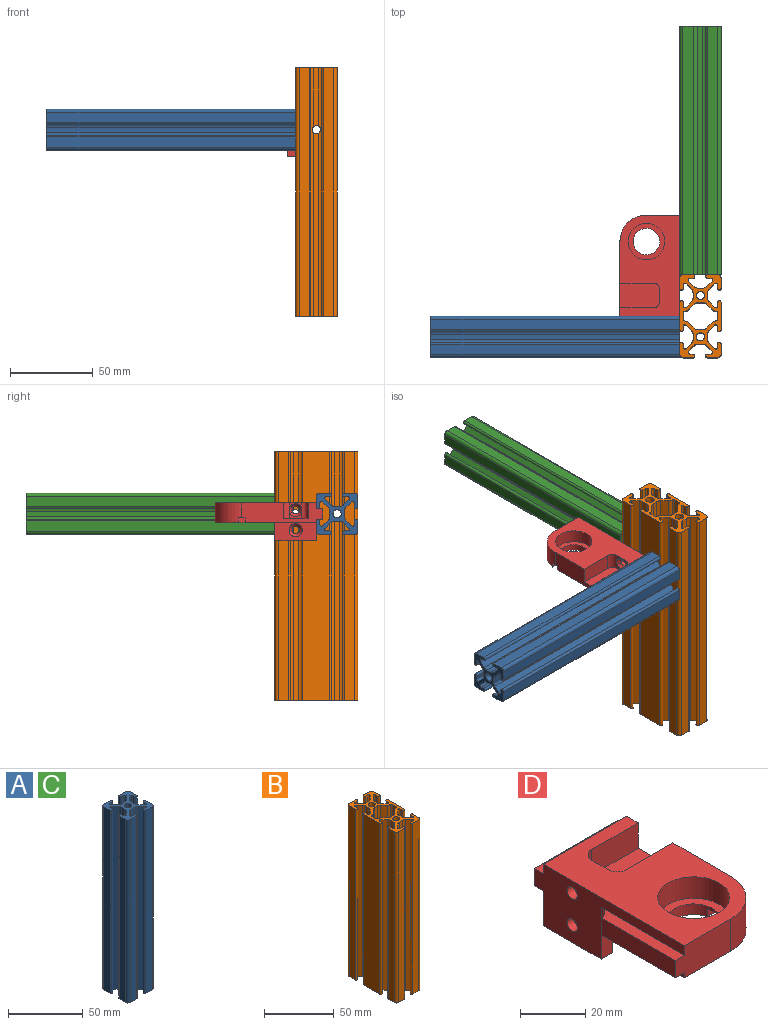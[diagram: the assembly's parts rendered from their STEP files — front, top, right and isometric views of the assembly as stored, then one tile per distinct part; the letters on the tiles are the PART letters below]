
ASSEMBLY  parts=4 mates=3
PART A: 59 faces, bbox 25x25x150 mm
  f0: plane 150x3.2mm, normal (-0.71,-0.71,0), area 679.2mm2, adj f28,f30,f57,f58
  f1: plane 150x2.08mm, normal (1,0,0), area 311.5mm2, adj f28,f29,f57,f58
  f2: plane 150x6.22mm, normal (-1,0,0), area 932.6mm2, adj f29,f55,f57,f58
  f3: plane 150x3.11mm, normal (-1,0,0), area 466.6mm2, adj f30,f31,f57,f58
  f4: plane 150x3.2mm, normal (-0.71,0.71,0), area 679.2mm2, adj f31,f32,f57,f58
  f5: plane 150x2.08mm, normal (1,0,0), area 311.5mm2, adj f32,f33,f57,f58
  f6: plane 150x6.22mm, normal (-1,0,0), area 932.6mm2, adj f33,f34,f57,f58
  f7: plane 150x6.15mm, normal (0,-1,0), area 922.4mm2, adj f34,f35,f57,f58
  f8: plane 150x2.03mm, normal (0,1,0), area 304.8mm2, adj f35,f36,f57,f58
  f9: plane 150x3.34mm, normal (0.71,-0.71,0), area 707.7mm2, adj f36,f37,f57,f58
  f10: plane 150x3.11mm, normal (0,-1,0), area 466.6mm2, adj f37,f38,f57,f58
  f11: plane 150x3.34mm, normal (-0.71,-0.71,0), area 707.7mm2, adj f38,f39,f57,f58
  f12: plane 150x2.03mm, normal (0,1,0), area 304.8mm2, adj f39,f40,f57,f58
  f13: plane 150x6.15mm, normal (0,-1,0), area 922.4mm2, adj f40,f41,f57,f58
  f14: plane 150x6.22mm, normal (1,0,0), area 932.6mm2, adj f41,f42,f57,f58
  f15: plane 150x2.08mm, normal (-1,0,0), area 311.5mm2, adj f42,f43,f57,f58
  f16: plane 150x3.2mm, normal (0.71,0.71,0), area 679.2mm2, adj f43,f44,f57,f58
  f17: plane 150x3.11mm, normal (1,0,0), area 466.6mm2, adj f44,f45,f57,f58
  f18: plane 150x3.2mm, normal (0.71,-0.71,0), area 679.2mm2, adj f45,f46,f57,f58
  f19: plane 150x2.08mm, normal (-1,0,0), area 311.5mm2, adj f46,f47,f57,f58
  f20: plane 150x6.22mm, normal (1,0,0), area 932.6mm2, adj f47,f48,f57,f58
  f21: plane 150x6.22mm, normal (0,1,0), area 932.6mm2, adj f48,f49,f57,f58
  f22: plane 150x2.1mm, normal (0,-1,0), area 315mm2, adj f49,f50,f57,f58
  f23: plane 150x3.34mm, normal (-0.71,0.71,0), area 707.7mm2, adj f50,f51,f57,f58
  f24: plane 150x3.11mm, normal (0,1,0), area 466.6mm2, adj f51,f52,f57,f58
  f25: plane 150x3.34mm, normal (0.71,0.71,0), area 707.7mm2, adj f52,f53,f57,f58
  f26: plane 150x2.1mm, normal (0,-1,0), area 315mm2, adj f53,f54,f57,f58
  f27: plane 150x6.22mm, normal (0,1,0), area 932.6mm2, adj f54,f55,f57,f58
  f28: cylinder r=1.01mm len=150mm, axis (0,0,-1), area 356.9mm2, adj f0,f1,f57,f58
  f29: cylinder r=1.07mm len=150mm, axis (0,0,-1), area 504.2mm2, adj f1,f2,f57,f58
  f30: cylinder r=3.33mm len=150mm, axis (0,0,-1), area 392.7mm2, adj f0,f3,f57,f58
  f31: cylinder r=3.33mm len=150mm, axis (0,0,-1), area 392.7mm2, adj f3,f4,f57,f58
  f32: cylinder r=1.01mm len=150mm, axis (0,0,-1), area 356.9mm2, adj f4,f5,f57,f58
  f33: cylinder r=1.07mm len=150mm, axis (0,0,-1), area 504.2mm2, adj f5,f6,f57,f58
  f34: cylinder r=1.96mm len=150mm, axis (0,0,-1), area 462.5mm2, adj f6,f7,f57,f58
  f35: cylinder r=1.07mm len=150mm, axis (0,0,-1), area 504.2mm2, adj f7,f8,f57,f58
  f36: cylinder r=1.01mm len=150mm, axis (0,0,-1), area 357.1mm2, adj f8,f9,f57,f58
  f37: cylinder r=3.17mm len=150mm, axis (0,0,-1), area 373.1mm2, adj f9,f10,f57,f58
  f38: cylinder r=3.17mm len=150mm, axis (0,0,-1), area 373.1mm2, adj f10,f11,f57,f58
  f39: cylinder r=1.01mm len=150mm, axis (0,0,-1), area 357.1mm2, adj f11,f12,f57,f58
  f40: cylinder r=1.07mm len=150mm, axis (0,0,-1), area 504.2mm2, adj f12,f13,f57,f58
  f41: cylinder r=1.96mm len=150mm, axis (0,0,-1), area 462.5mm2, adj f13,f14,f57,f58
  f42: cylinder r=1.07mm len=150mm, axis (0,0,-1), area 504.2mm2, adj f14,f15,f57,f58
  f43: cylinder r=1.01mm len=150mm, axis (0,0,-1), area 356.9mm2, adj f15,f16,f57,f58
  f44: cylinder r=3.33mm len=150mm, axis (0,0,-1), area 392.7mm2, adj f16,f17,f57,f58
  f45: cylinder r=3.33mm len=150mm, axis (0,0,-1), area 392.7mm2, adj f17,f18,f57,f58
  f46: cylinder r=1.01mm len=150mm, axis (0,0,-1), area 356.9mm2, adj f18,f19,f57,f58
  f47: cylinder r=1.07mm len=150mm, axis (0,0,-1), area 504.2mm2, adj f19,f20,f57,f58
  f48: cylinder r=1.96mm len=150mm, axis (0,0,-1), area 462.5mm2, adj f20,f21,f57,f58
  f49: cylinder r=1.07mm len=150mm, axis (0,0,-1), area 504.2mm2, adj f21,f22,f57,f58
  f50: cylinder r=1.01mm len=150mm, axis (0,0,-1), area 357.1mm2, adj f22,f23,f57,f58
  f51: cylinder r=3.17mm len=150mm, axis (0,0,-1), area 373.1mm2, adj f23,f24,f57,f58
  f52: cylinder r=3.17mm len=150mm, axis (0,0,-1), area 373.1mm2, adj f24,f25,f57,f58
  f53: cylinder r=1.01mm len=150mm, axis (0,0,-1), area 357.1mm2, adj f25,f26,f57,f58
  f54: cylinder r=1.07mm len=150mm, axis (0,0,-1), area 504.2mm2, adj f26,f27,f57,f58
  f55: cylinder r=1.96mm len=150mm, axis (0,0,-1), area 462.5mm2, adj f2,f27,f57,f58
  f56: cylinder r=2.5mm len=150mm, axis (0,0,-1), area 2356.2mm2, adj f57,f58
  f57: plane 25x25mm, normal (0,0,1), area 274.7mm2, adj f0,f1,f2,f3,f4,f5,f6,f7
  f58: plane 25x25mm, normal (0,0,-1), area 274.7mm2, adj f0,f1,f2,f3,f4,f5,f6,f7
PART B: 126 faces, bbox 25x50x150 mm
  f0: plane 110.56x3.15mm, normal (0,1,0), area 346.8mm2, adj f90,f91,f123,f124
  f1: plane 110.56x3.15mm, normal (0,-1,0), area 346.8mm2, adj f103,f104,f122,f124
  f2: plane 110.56x3.15mm, normal (-1,0,0), area 346.8mm2, adj f57,f58,f117,f124
  f3: plane 110.56x3.15mm, normal (-1,0,0), area 346.8mm2, adj f63,f64,f119,f124
  f4: plane 150x0.24mm, normal (0,-1,0), area 36.3mm2, adj f54,f105,f124,f125
  f5: plane 150x4.34mm, normal (1,0,0), area 651mm2, adj f54,f95,f124,f125
  f6: plane 150x6.15mm, normal (-1,0,0), area 922.3mm2, adj f55,f94,f124,f125
  f7: plane 150x2.11mm, normal (1,0,0), area 316.2mm2, adj f55,f56,f124,f125
  f8: plane 150x3.32mm, normal (-0.71,-0.71,0), area 704.6mm2, adj f56,f57,f124,f125
  f9: plane 150x3.32mm, normal (-0.71,0.71,0), area 704.6mm2, adj f58,f59,f124,f125
  f10: plane 150x2.11mm, normal (1,0,0), area 316.2mm2, adj f59,f60,f124,f125
  f11: plane 150x16.36mm, normal (-1,0,0), area 2454mm2, adj f60,f61,f124,f125
  f12: plane 150x2.11mm, normal (1,0,0), area 316.2mm2, adj f61,f62,f124,f125
  f13: plane 150x3.32mm, normal (-0.71,-0.71,0), area 704.6mm2, adj f62,f63,f124,f125
  f14: plane 150x3.32mm, normal (-0.71,0.71,0), area 704.6mm2, adj f64,f65,f124,f125
  f15: plane 150x2.11mm, normal (1,0,0), area 316.2mm2, adj f65,f66,f124,f125
  f16: plane 150x6.15mm, normal (-1,0,0), area 922.3mm2, adj f66,f67,f124,f125
  f17: plane 150x6.15mm, normal (0,-1,0), area 922.3mm2, adj f67,f68,f124,f125
  f18: plane 150x2.11mm, normal (0,1,0), area 316.2mm2, adj f68,f69,f124,f125
  f19: plane 150x3.32mm, normal (0.71,-0.71,0), area 704.6mm2, adj f69,f70,f124,f125
  f20: plane 110.56x3.15mm, normal (0,-1,0), area 346.8mm2, adj f70,f71,f120,f124
  f21: plane 150x3.32mm, normal (-0.71,-0.71,0), area 704.6mm2, adj f71,f72,f124,f125
  f22: plane 150x2.11mm, normal (0,1,0), area 316.2mm2, adj f72,f73,f124,f125
  f23: plane 150x6.15mm, normal (0,-1,0), area 922.3mm2, adj f73,f74,f124,f125
  f24: plane 150x6.15mm, normal (1,0,0), area 922.3mm2, adj f74,f75,f124,f125
  f25: plane 150x2.11mm, normal (-1,0,0), area 316.2mm2, adj f75,f76,f124,f125
  f26: plane 150x3.32mm, normal (0.71,0.71,0), area 704.6mm2, adj f76,f77,f124,f125
  f27: plane 110.56x3.15mm, normal (1,0,0), area 346.8mm2, adj f77,f78,f118,f124
  f28: plane 150x3.32mm, normal (0.71,-0.71,0), area 704.6mm2, adj f78,f79,f124,f125
  f29: plane 150x2.11mm, normal (-1,0,0), area 316.2mm2, adj f79,f80,f124,f125
  f30: plane 150x16.36mm, normal (1,0,0), area 2454mm2, adj f80,f81,f124,f125
  f31: plane 150x2.11mm, normal (-1,0,0), area 316.2mm2, adj f81,f82,f124,f125
  f32: plane 150x3.32mm, normal (0.71,0.71,0), area 704.6mm2, adj f82,f83,f124,f125
  f33: plane 110.56x3.15mm, normal (1,0,0), area 346.8mm2, adj f83,f84,f116,f124
  f34: plane 150x3.32mm, normal (0.71,-0.71,0), area 704.6mm2, adj f84,f85,f124,f125
  f35: plane 150x2.11mm, normal (-1,0,0), area 316.2mm2, adj f85,f86,f124,f125
  f36: plane 150x6.15mm, normal (1,0,0), area 922.3mm2, adj f86,f87,f124,f125
  f37: plane 150x6.15mm, normal (0,1,0), area 922.3mm2, adj f87,f88,f124,f125
  f38: plane 150x2.11mm, normal (0,-1,0), area 316.2mm2, adj f88,f89,f124,f125
  f39: plane 150x3.32mm, normal (-0.71,0.71,0), area 704.6mm2, adj f89,f90,f124,f125
  f40: plane 150x3.32mm, normal (0.71,0.71,0), area 704.6mm2, adj f91,f92,f124,f125
  f41: plane 150x2.11mm, normal (0,-1,0), area 316.2mm2, adj f92,f93,f124,f125
  f42: plane 150x6.15mm, normal (0,1,0), area 922.3mm2, adj f93,f94,f124,f125
  f43: plane 150x0.24mm, normal (0,1,0), area 36.3mm2, adj f95,f96,f124,f125
  f44: plane 150x3.32mm, normal (0.71,0.71,0), area 704.6mm2, adj f96,f97,f124,f125
  f45: plane 110.56x3.15mm, normal (0,1,0), area 346.8mm2, adj f97,f98,f121,f124
  f46: plane 150x3.32mm, normal (-0.71,0.71,0), area 704.6mm2, adj f98,f99,f124,f125
  f47: plane 150x0.24mm, normal (0,1,0), area 36.3mm2, adj f99,f100,f124,f125
  f48: plane 150x4.34mm, normal (-1,0,0), area 651mm2, adj f100,f101,f124,f125
  f49: plane 150x0.24mm, normal (0,-1,0), area 36.3mm2, adj f101,f102,f124,f125
  f50: plane 150x3.32mm, normal (-0.71,-0.71,0), area 704.6mm2, adj f102,f103,f124,f125
  f51: plane 150x3.32mm, normal (0.71,-0.71,0), area 704.6mm2, adj f104,f105,f124,f125
  f52: cylinder r=2.5mm len=110.73mm, axis (0,0,-1), area 1731.8mm2, adj f118,f119,f120,f121,f124
  f53: cylinder r=2.5mm len=110.73mm, axis (0,0,-1), area 1731.8mm2, adj f116,f117,f122,f123,f124
  f54: cylinder r=0.76mm len=150mm, axis (0,0,-1), area 179.1mm2, adj f4,f5,f124,f125
  f55: cylinder r=1.07mm len=150mm, axis (0,0,-1), area 504.2mm2, adj f6,f7,f124,f125
  f56: cylinder r=1mm len=150mm, axis (0,0,-1), area 354.1mm2, adj f7,f8,f124,f125
  f57: cylinder r=3.17mm len=150mm, axis (0,0,-1), area 370.9mm2, adj f2,f8,f110,f117,f124,f125
  f58: cylinder r=3.17mm len=150mm, axis (0,0,-1), area 370.9mm2, adj f2,f9,f110,f117,f124,f125
  f59: cylinder r=1mm len=150mm, axis (0,0,-1), area 354.1mm2, adj f9,f10,f124,f125
  f60: cylinder r=1.07mm len=150mm, axis (0,0,-1), area 504.2mm2, adj f10,f11,f124,f125
  f61: cylinder r=1.07mm len=150mm, axis (0,0,-1), area 504.2mm2, adj f11,f12,f124,f125
  f62: cylinder r=1mm len=150mm, axis (0,0,-1), area 354.1mm2, adj f12,f13,f124,f125
  f63: cylinder r=3.17mm len=150mm, axis (0,0,-1), area 370.9mm2, adj f3,f13,f111,f119,f124,f125
  f64: cylinder r=3.17mm len=150mm, axis (0,0,-1), area 370.9mm2, adj f3,f14,f111,f119,f124,f125
  f65: cylinder r=1mm len=150mm, axis (0,0,-1), area 354.1mm2, adj f14,f15,f124,f125
  f66: cylinder r=1.07mm len=150mm, axis (0,0,-1), area 504.2mm2, adj f15,f16,f124,f125
  f67: cylinder r=2.03mm len=150mm, axis (0,0,-1), area 478.6mm2, adj f16,f17,f124,f125
  f68: cylinder r=1.07mm len=150mm, axis (0,0,-1), area 504.2mm2, adj f17,f18,f124,f125
  f69: cylinder r=1mm len=150mm, axis (0,0,-1), area 354.1mm2, adj f18,f19,f124,f125
  f70: cylinder r=3.17mm len=150mm, axis (0,0,-1), area 370.9mm2, adj f19,f20,f106,f120,f124,f125
  f71: cylinder r=3.17mm len=150mm, axis (0,0,-1), area 370.9mm2, adj f20,f21,f106,f120,f124,f125
  f72: cylinder r=1mm len=150mm, axis (0,0,-1), area 354.1mm2, adj f21,f22,f124,f125
  f73: cylinder r=1.07mm len=150mm, axis (0,0,-1), area 504.2mm2, adj f22,f23,f124,f125
  f74: cylinder r=2.03mm len=150mm, axis (0,0,-1), area 478.6mm2, adj f23,f24,f124,f125
  f75: cylinder r=1.07mm len=150mm, axis (0,0,-1), area 504.2mm2, adj f24,f25,f124,f125
  f76: cylinder r=1mm len=150mm, axis (0,0,-1), area 354.1mm2, adj f25,f26,f124,f125
  f77: cylinder r=3.17mm len=150mm, axis (0,0,-1), area 370.9mm2, adj f26,f27,f108,f118,f124,f125
  f78: cylinder r=3.17mm len=150mm, axis (0,0,-1), area 370.9mm2, adj f27,f28,f108,f118,f124,f125
  f79: cylinder r=1mm len=150mm, axis (0,0,-1), area 354.1mm2, adj f28,f29,f124,f125
  f80: cylinder r=1.07mm len=150mm, axis (0,0,-1), area 504.2mm2, adj f29,f30,f124,f125
  f81: cylinder r=1.07mm len=150mm, axis (0,0,-1), area 504.2mm2, adj f30,f31,f124,f125
  f82: cylinder r=1mm len=150mm, axis (0,0,-1), area 354.1mm2, adj f31,f32,f124,f125
  f83: cylinder r=3.17mm len=150mm, axis (0,0,-1), area 370.9mm2, adj f32,f33,f109,f116,f124,f125
  f84: cylinder r=3.17mm len=150mm, axis (0,0,-1), area 370.9mm2, adj f33,f34,f109,f116,f124,f125
  f85: cylinder r=1mm len=150mm, axis (0,0,-1), area 354.1mm2, adj f34,f35,f124,f125
  f86: cylinder r=1.07mm len=150mm, axis (0,0,-1), area 504.2mm2, adj f35,f36,f124,f125
  f87: cylinder r=2.03mm len=150mm, axis (0,0,-1), area 478.6mm2, adj f36,f37,f124,f125
  f88: cylinder r=1.07mm len=150mm, axis (0,0,-1), area 504.2mm2, adj f37,f38,f124,f125
  f89: cylinder r=1mm len=150mm, axis (0,0,-1), area 354.1mm2, adj f38,f39,f124,f125
  f90: cylinder r=3.17mm len=150mm, axis (0,0,-1), area 370.9mm2, adj f0,f39,f112,f123,f124,f125
  f91: cylinder r=3.17mm len=150mm, axis (0,0,-1), area 370.9mm2, adj f0,f40,f112,f123,f124,f125
  f92: cylinder r=1mm len=150mm, axis (0,0,-1), area 354.1mm2, adj f40,f41,f124,f125
  f93: cylinder r=1.07mm len=150mm, axis (0,0,-1), area 504.2mm2, adj f41,f42,f124,f125
  f94: cylinder r=2.03mm len=150mm, axis (0,0,-1), area 478.6mm2, adj f6,f42,f124,f125
  f95: cylinder r=0.76mm len=150mm, axis (0,0,-1), area 179.1mm2, adj f5,f43,f124,f125
  f96: cylinder r=3.14mm len=150mm, axis (0,0,-1), area 370.1mm2, adj f43,f44,f124,f125
  f97: cylinder r=3.17mm len=150mm, axis (0,0,-1), area 370.9mm2, adj f44,f45,f107,f121,f124,f125
  f98: cylinder r=3.17mm len=150mm, axis (0,0,-1), area 370.9mm2, adj f45,f46,f107,f121,f124,f125
  f99: cylinder r=3.14mm len=150mm, axis (0,0,-1), area 370.1mm2, adj f46,f47,f124,f125
  f100: cylinder r=0.76mm len=150mm, axis (0,0,-1), area 179.1mm2, adj f47,f48,f124,f125
  f101: cylinder r=0.76mm len=150mm, axis (0,0,-1), area 179.1mm2, adj f48,f49,f124,f125
  f102: cylinder r=3.14mm len=150mm, axis (0,0,-1), area 370.1mm2, adj f49,f50,f124,f125
  f103: cylinder r=3.17mm len=150mm, axis (0,0,-1), area 370.9mm2, adj f1,f50,f115,f122,f124,f125
  f104: cylinder r=3.17mm len=150mm, axis (0,0,-1), area 370.9mm2, adj f1,f51,f115,f122,f124,f125
  f105: cylinder r=3.14mm len=150mm, axis (0,0,-1), area 370.1mm2, adj f4,f51,f124,f125
  f106: plane 35.56x3.15mm, normal (0,-1,0), area 110.7mm2, adj f70,f71,f120,f125
  f107: plane 35.56x3.15mm, normal (0,1,0), area 110.7mm2, adj f97,f98,f121,f125
  f108: plane 35.56x3.15mm, normal (1,0,0), area 110.7mm2, adj f77,f78,f118,f125
  f109: plane 35.56x3.15mm, normal (1,0,0), area 110.7mm2, adj f83,f84,f116,f125
  f110: plane 35.56x3.15mm, normal (-1,0,0), area 110.7mm2, adj f57,f58,f117,f125
  f111: plane 35.56x3.15mm, normal (-1,0,0), area 110.7mm2, adj f63,f64,f119,f125
  f112: plane 35.56x3.15mm, normal (0,1,0), area 110.7mm2, adj f90,f91,f123,f125
  f113: cylinder r=2.5mm len=35.73mm, axis (0,0,-1), area 553.7mm2, adj f118,f119,f120,f121,f125
  f114: cylinder r=2.5mm len=35.73mm, axis (0,0,-1), area 553.7mm2, adj f116,f117,f122,f123,f125
  f115: plane 35.56x3.15mm, normal (0,-1,0), area 110.7mm2, adj f103,f104,f122,f125
  f116: cylinder r=2.5mm len=5mm, axis (1,0,0), area 34.4mm2, adj f33,f53,f83,f84,f109,f114,f122,f123
  f117: cylinder r=2.5mm len=5mm, axis (1,0,0), area 34.4mm2, adj f2,f53,f57,f58,f110,f114,f122,f123
  f118: cylinder r=2.5mm len=5mm, axis (1,0,0), area 34.4mm2, adj f27,f52,f77,f78,f108,f113,f120,f121
  f119: cylinder r=2.5mm len=5mm, axis (1,0,0), area 34.4mm2, adj f3,f52,f63,f64,f111,f113,f120,f121
  f120: cylinder r=2.5mm len=5mm, axis (0,1,0), area 34.4mm2, adj f20,f52,f70,f71,f106,f113,f118,f119
  f121: cylinder r=2.5mm len=5mm, axis (0,1,0), area 34.4mm2, adj f45,f52,f97,f98,f107,f113,f118,f119
  f122: cylinder r=2.5mm len=5mm, axis (0,1,0), area 34.4mm2, adj f1,f53,f103,f104,f114,f115,f116,f117
  f123: cylinder r=2.5mm len=5mm, axis (0,1,0), area 34.4mm2, adj f0,f53,f90,f91,f112,f114,f116,f117
  f124: plane 50x25mm, normal (0,0,-1), area 481.7mm2, adj f0,f1,f2,f3,f4,f5,f6,f7
  f125: plane 50x25mm, normal (0,0,1), area 481.7mm2, adj f4,f5,f6,f7,f8,f9,f10,f11
PART C: same geometry as A
PART D: 41 faces, bbox 42.9x67.9x25.9 mm
  f0: plane 7x2.69mm, normal (1,0,0), area 8.2mm2, adj f12,f31,f32,f35
  f1: plane 11x5mm, normal (0,-1,0), area 55mm2, adj f2,f3,f6,f24
  f2: plane 25x11mm, normal (1,0,0), area 226.3mm2, adj f1,f4,f6,f24,f33
  f3: plane 65x23mm, normal (-1,0,0), area 771.8mm2, adj f1,f4,f6,f7,f10,f12,f14,f15
  f4: plane 36x13mm, normal (0,1,0), area 127mm2, adj f2,f3,f6,f8,f23,f24
  f5: cylinder r=8mm len=16mm, axis (0,0,1), area 188.9mm2, adj f6,f13,f20,f21,f22
  f6: plane 61x36mm, normal (0,0,-1), area 1782.7mm2, adj f1,f2,f3,f4,f5,f8,f9,f10
  f7: plane 36x3.6mm, normal (0,1,0), area 129.6mm2, adj f3,f8,f12,f19
  f8: plane 49x12mm, normal (1,0,0), area 417.1mm2, adj f4,f6,f7,f9,f12,f18,f19,f21
  f9: cylinder r=16mm len=16mm, axis (0,0,-1), area 295.6mm2, adj f6,f8,f10,f12,f20,f22
  f10: plane 24x12mm, normal (0,-1,0), area 265.6mm2, adj f3,f6,f9,f12,f14,f15,f16
  f11: cylinder r=11mm len=22mm, axis (0,0,-1), area 552.9mm2, adj f12,f13
  f12: plane 61x36mm, normal (0,0,1), area 1407.8mm2, adj f0,f3,f7,f8,f9,f10,f11,f27
  f13: plane 22x22mm, normal (0,0,1), area 179.1mm2, adj f5,f11
  f14: plane 36x4mm, normal (0,0,-1), area 131.4mm2, adj f3,f10,f16,f17
  f15: plane 36x4mm, normal (0,0,1), area 131.4mm2, adj f3,f10,f16,f17
  f16: plane 32x6.4mm, normal (-1,0,0), area 204.8mm2, adj f10,f14,f15,f17
  f17: cylinder r=4mm len=6.4mm, axis (0,0,1), area 40.2mm2, adj f3,f14,f15,f16
  f18: plane 36x6.4mm, normal (0,1,0), area 230.4mm2, adj f3,f8,f19,f23
  f19: plane 36x4mm, normal (0,0,1), area 144mm2, adj f3,f7,f8,f18
  f20: plane 8.13x3mm, normal (0,1,0), area 24.4mm2, adj f5,f6,f9,f22
  f21: plane 8.25x3mm, normal (0,-1,0), area 24.8mm2, adj f5,f6,f8,f22
  f22: plane 8.25x4mm, normal (0,0,-1), area 32.3mm2, adj f5,f8,f9,f20,f21
  f23: plane 36x4mm, normal (0,0,-1), area 144mm2, adj f3,f4,f8,f18
  f24: plane 25x5mm, normal (0,0,-1), area 125mm2, adj f1,f2,f3,f4
  f25: cylinder r=2.2mm len=4.4mm, axis (1,0,0), area 41.5mm2, adj f3,f33
  f26: cylinder r=2.2mm len=10mm, axis (1,0,0), area 138.2mm2, adj f3,f34,f35,f36,f37
  f27: plane 20x9.5mm, normal (0,1,0), area 190mm2, adj f8,f12,f28,f32
  f28: plane 24x15mm, normal (0,0,1), area 353.1mm2, adj f8,f27,f29,f30,f31,f32
  f29: plane 20x9.5mm, normal (0,-1,0), area 190mm2, adj f8,f12,f28,f31
  f30: plane 7x3.19mm, normal (1,0,0), area 11.7mm2, adj f28,f31,f32,f36
  f31: cylinder r=4mm len=9.5mm, axis (0,0,1), area 59mm2, adj f0,f12,f28,f29,f30,f34
  f32: cylinder r=4mm len=9.5mm, axis (0,0,-1), area 59mm2, adj f0,f12,f27,f28,f30,f37
  f33: cone r=2.2mm half-angle=41deg, axis (1,0,0), area 51.1mm2, adj f2,f25
  f34: bspline ~3.61x2.01mm, area 7.5mm2, adj f26,f31,f35,f36
  f35: cone r=2.2mm half-angle=41deg, axis (1,0,0), area 17.8mm2, adj f0,f26,f34,f37
  f36: cone r=2.2mm half-angle=41deg, axis (1,0,0), area 17.8mm2, adj f26,f30,f34,f37
  f37: bspline ~3.61x2.01mm, area 7.5mm2, adj f26,f32,f35,f36
  f38: cone r=2.2mm half-angle=41deg, axis (1,0,0), area 0mm2, adj f39,f40
  f39: plane 5.64x1.48mm, normal (-1,0,0), area 3.3mm2, adj f38,f40
  f40: plane 7.97x3.94mm, normal (0,0,1), area 3.6mm2, adj f38,f39
PLACE A rot(axis=(0.71,0,-0.71),180deg) t=(-137.5,175,-1057.5)mm
PLACE B at identity
PLACE C rot(axis=(1,0,0),90deg) t=(50,87.5,-1157.5)mm
PLACE D rot(axis=(0,0,1),180deg) t=(50,200,-1013.82)mm
MATE fastened D.f3 <-> C.f6  axis (1,0,0) through (37.5,112.5,-1060.82)mm
MATE fastened C.f56 <-> B.f120  axis (0,-1,0) through (50,112.5,-1057.5)mm
MATE fastened A.f56 <-> B.f118  axis (1,0,0) through (37.5,75,-1057.5)mm
